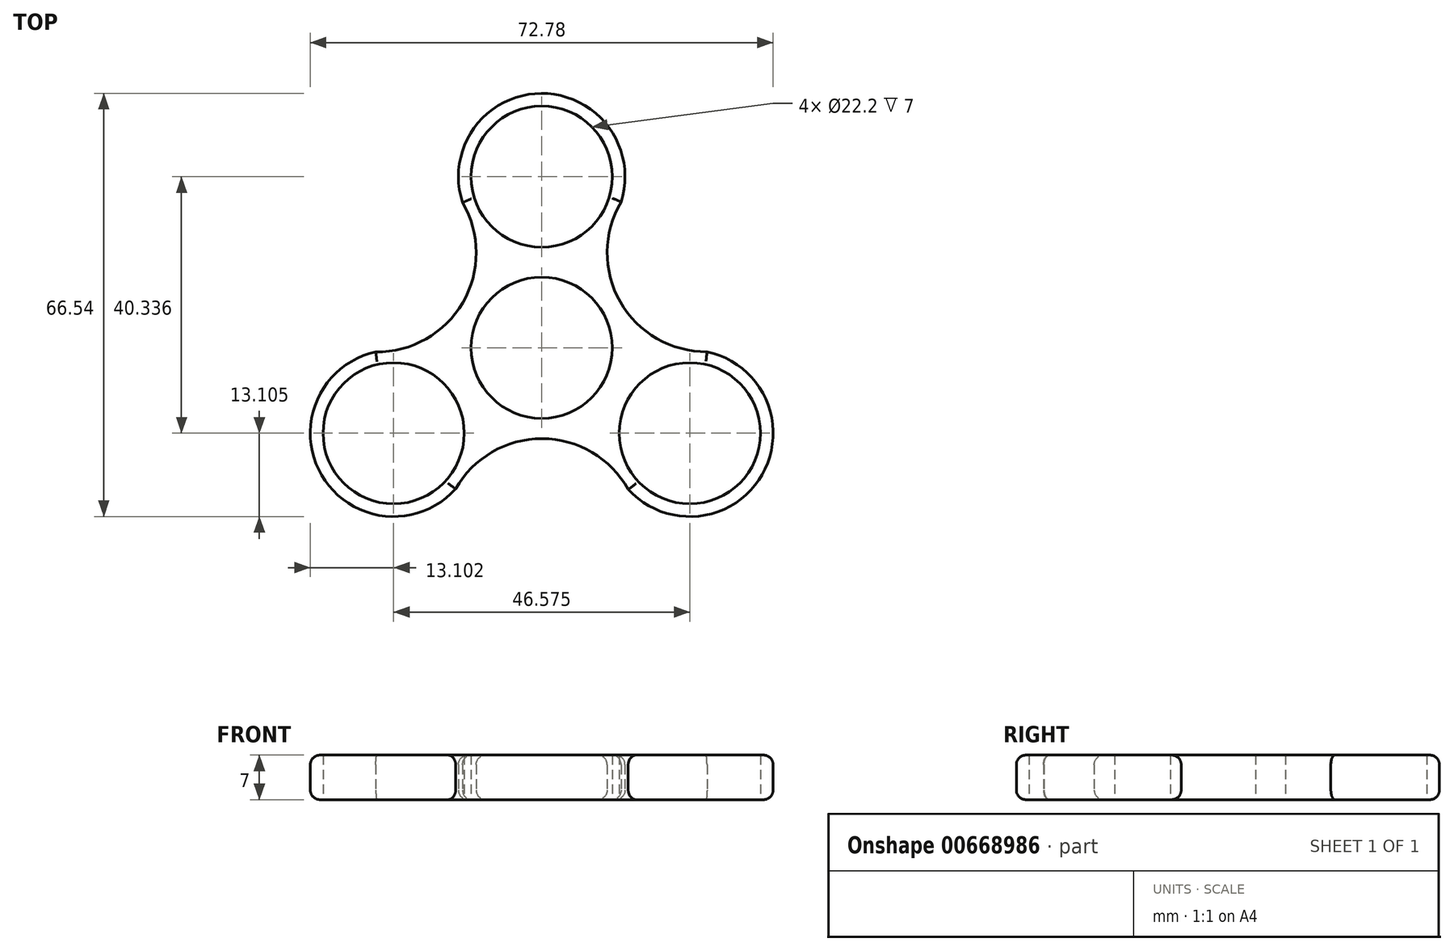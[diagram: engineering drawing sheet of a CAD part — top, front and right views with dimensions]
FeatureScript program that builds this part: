
annotation { "Feature Type Name" : "Feature", "Feature Type Description" : "" }
export const myFeature = defineFeature(function(context is Context, id is Id, definition is map)
    precondition{}
    {
        {
            var Q0;
            Q0=qCreatedBy(makeId("Top.planeOp"),FACE);
            var sketch = newSketch(context, id + "F0", { "sketchPlane" : qUnion([Q0])});
            skCircle(sketch, "E0", {"center": v(0, 0) * mm, "radius": 11.1 * mm});
            skSolve(sketch);
        }
        {
            var Q0;
            Q0=makeQuery(id+"F0.imprint","IMPRINT",FACE,{"disambiguationData":[TD([[makeQuery(id+"F0.imprint","IMPRINT",EDGE,{"derivedFrom":sQuery(id+"F0.wireOp",EDGE,"E0")}),1.0]])]});
            var sketch = newSketch(context, id + "F1", { "sketchPlane" : qUnion([Q0])});
            skCircle(sketch, "E1", {"center": v(0, 26.9) * mm, "radius": 11.1 * mm});
            skArc(sketch, "E2", {"start": v(11.12, 19.97) * mm, "mid": v(0.04, 40) * mm, "end": v(-11.16, 20.04) * mm});
            skCircle(sketch, "E3.1.0", {"center": v(-23.29, -13.45) * mm, "radius": 11.1 * mm});
            skArc(sketch, "E3.1.1", {"start": v(-22.85, -0.35) * mm, "mid": v(-34.65, -19.96) * mm, "end": v(-11.77, -19.69) * mm});
            skCircle(sketch, "E3.2.0", {"center": v(23.29, -13.45) * mm, "radius": 11.1 * mm});
            skArc(sketch, "E3.2.1", {"start": v(11.73, -19.61) * mm, "mid": v(34.61, -20.03) * mm, "end": v(22.93, -0.35) * mm});
            skPoint(sketch, "E3.center", {"position": v(0, 0) * mm});
            skLineSegment(sketch, "E4", {"start": v(-13.67, -7.9) * mm, "end": v(-11.94, -6.9) * mm, "construction": true});
            skArc(sketch, "E5", {"start": v(12.48, 22.92) * mm, "mid": v(12.36, 7.2) * mm, "end": v(26, -0.63) * mm});
            skArc(sketch, "E6.1.0", {"start": v(-26.09, -0.65) * mm, "mid": v(-12.4, 7.1) * mm, "end": v(-12.45, 22.82) * mm});
            skArc(sketch, "E6.2.0", {"start": v(13.6, -22.27) * mm, "mid": v(0.05, -14.3) * mm, "end": v(-13.54, -22.2) * mm});
            skLineSegment(sketch, "E7.trimOffspring", {"start": v(11.64, 6.72) * mm, "end": v(12.38, 7.15) * mm, "construction": true});
            skLineSegment(sketch, "E8.trimOffspring", {"start": v(16.74, -2.1) * mm, "end": v(17.74, -3.83) * mm, "construction": true});
            skSolve(sketch);
        }
        {
            var Q0;
            Q0=makeQuery(id+"F1.imprint","IMPRINT",FACE,{"disambiguationData":[TD([[makeQuery(id+"F1.imprint","IMPRINT",EDGE,{"derivedFrom":sQuery(id+"F1.wireOp",EDGE,"E1")}),-1.0]])]});
            extrude(context, id + "F2", {"entities" : qUnion([Q0]), "depth" : 7 * mm, "offsetDistance" : 25 * mm});
        }
        {
            var Q0;
            Q0=makeQuery(id+"F2.opExtrude","CAP_EDGE",EDGE,{"disambiguationData":[OSD([sQuery(id+"F1.wireOp",EDGE,"E3.1.1")])],"isStart":false});
            var Q1;
            Q1=makeQuery(id+"F2.opExtrude","CAP_EDGE",EDGE,{"disambiguationData":[OSD([sQuery(id+"F1.wireOp",EDGE,"E6.2.0")])],"isStart":false});
            var Q2;
            Q2=makeQuery(id+"F2.opExtrude","CAP_EDGE",EDGE,{"disambiguationData":[OSD([sQuery(id+"F1.wireOp",EDGE,"E6.1.0")])],"isStart":false});
            var Q3;
            Q3=makeQuery(id+"F2.opExtrude","CAP_EDGE",EDGE,{"disambiguationData":[OSD([sQuery(id+"F1.wireOp",EDGE,"E5")])],"isStart":false});
            var Q4;
            Q4=makeQuery(id+"F2.opExtrude","CAP_EDGE",EDGE,{"disambiguationData":[OSD([sQuery(id+"F1.wireOp",EDGE,"E2")])],"isStart":false});
            var Q5;
            Q5=makeQuery(id+"F2.opExtrude","CAP_EDGE",EDGE,{"disambiguationData":[OSD([sQuery(id+"F1.wireOp",EDGE,"E3.2.1")])],"isStart":false});
            fillet(context, id + "F3", {"entities" : qUnion([Q0, Q1, Q2, Q3, Q4, Q5]), "radius" : 1.5 * mm, "tangentPropagation" : true, "allowEdgeOverflow" : false});
        }
        {
            var Q0;
            Q0=makeQuery(id+"F2.opExtrude","CAP_EDGE",EDGE,{"disambiguationData":[OSD([sQuery(id+"F1.wireOp",EDGE,"E5")])],"isStart":true});
            var Q1;
            Q1=makeQuery(id+"F2.opExtrude","CAP_EDGE",EDGE,{"disambiguationData":[OSD([sQuery(id+"F1.wireOp",EDGE,"E6.1.0")])],"isStart":true});
            var Q2;
            Q2=makeQuery(id+"F2.opExtrude","CAP_EDGE",EDGE,{"disambiguationData":[OSD([sQuery(id+"F1.wireOp",EDGE,"E6.2.0")])],"isStart":true});
            var Q3;
            Q3=makeQuery(id+"F2.opExtrude","CAP_EDGE",EDGE,{"disambiguationData":[OSD([sQuery(id+"F1.wireOp",EDGE,"E3.2.1")])],"isStart":true});
            var Q4;
            Q4=makeQuery(id+"F2.opExtrude","CAP_EDGE",EDGE,{"disambiguationData":[OSD([sQuery(id+"F1.wireOp",EDGE,"E2")])],"isStart":true});
            var Q5;
            Q5=makeQuery(id+"F2.opExtrude","CAP_EDGE",EDGE,{"disambiguationData":[OSD([sQuery(id+"F1.wireOp",EDGE,"E3.1.1")])],"isStart":true});
            fillet(context, id + "F4", {"entities" : qUnion([Q0, Q1, Q2, Q3, Q4, Q5]), "radius" : 1.5 * mm, "tangentPropagation" : true, "allowEdgeOverflow" : false});
        }
    });
